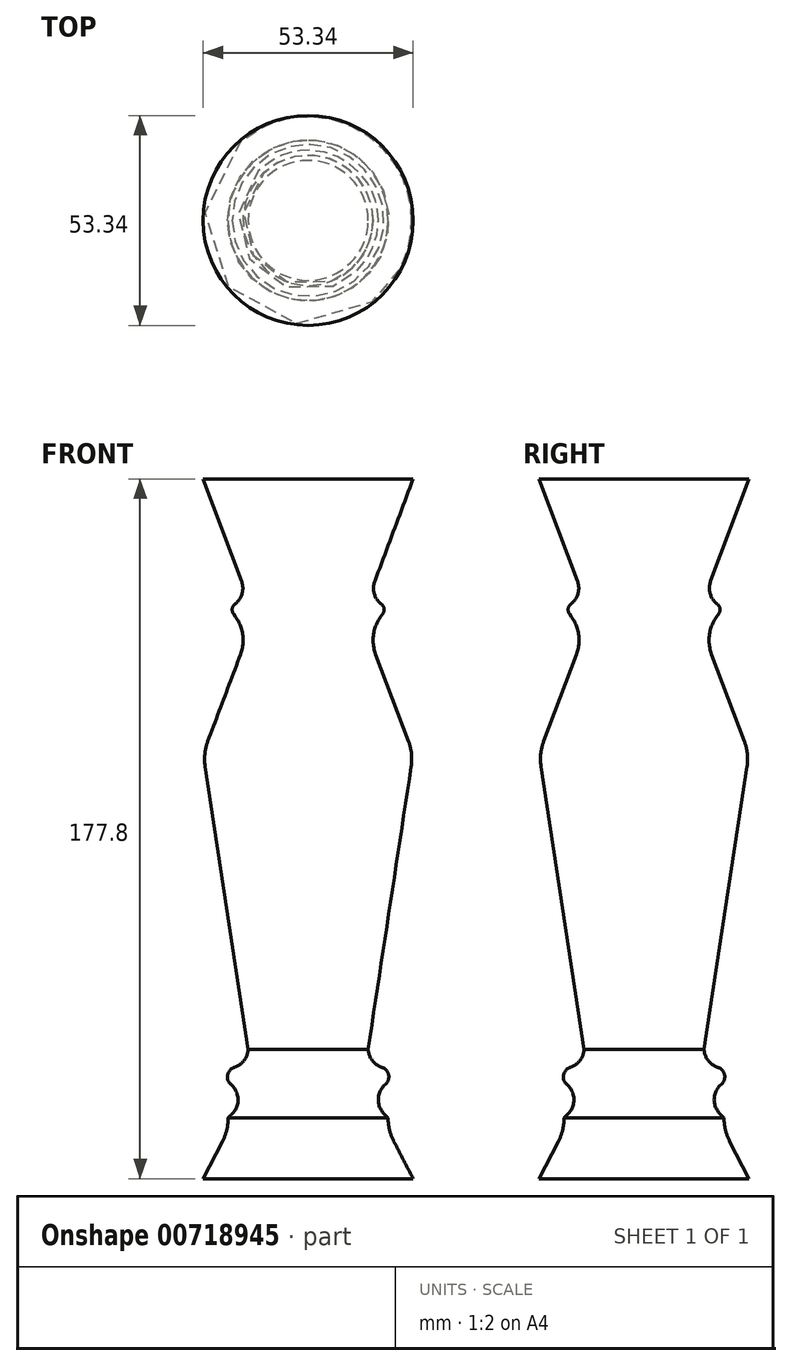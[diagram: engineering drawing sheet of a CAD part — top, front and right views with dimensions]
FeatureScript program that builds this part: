
annotation { "Feature Type Name" : "Feature", "Feature Type Description" : "" }
export const myFeature = defineFeature(function(context is Context, id is Id, definition is map)
    precondition{}
    {
        {
            var Q0;
            Q0=qCreatedBy(makeId("Front.planeOp"),FACE);
            var sketch = newSketch(context, id + "F0", { "sketchPlane" : qUnion([Q0])});
            skLineSegment(sketch, "E0", {"start": v(0, 90.6) * mm, "end": v(26.67, 90.6) * mm});
            skLineSegment(sketch, "E1", {"start": v(26.67, 90.6) * mm, "end": v(15.24, 60.11) * mm});
            skLineSegment(sketch, "E2", {"start": v(15.24, 60.11) * mm, "end": v(20.32, 58.2) * mm});
            skLineSegment(sketch, "E3", {"start": v(20.32, 58.2) * mm, "end": v(15.24, 51.1) * mm});
            skLineSegment(sketch, "E4", {"start": v(15.24, 51.1) * mm, "end": v(25.5, 23.91) * mm});
            skLineSegment(sketch, "E5", {"start": v(26.17, 17.52) * mm, "end": v(15.24, -54.38) * mm});
            skLineSegment(sketch, "E6", {"start": v(15.24, -54.38) * mm, "end": v(15.24, -54.38) * mm});
            skLineSegment(sketch, "E7", {"start": v(15.24, -54.38) * mm, "end": v(15.24, -59.17) * mm});
            skLineSegment(sketch, "E8", {"start": v(15.24, -59.17) * mm, "end": v(21.59, -59.17) * mm});
            skLineSegment(sketch, "E9", {"start": v(21.59, -59.17) * mm, "end": v(21.59, -61.6) * mm});
            skLineSegment(sketch, "E10", {"start": v(21.59, -61.6) * mm, "end": v(15.24, -67) * mm});
            skLineSegment(sketch, "E11", {"start": v(15.24, -67) * mm, "end": v(20.32, -71.7) * mm});
            skLineSegment(sketch, "E12", {"start": v(20.32, -71.7) * mm, "end": v(20.32, -71.86) * mm});
            skLineSegment(sketch, "E13", {"start": v(21.74, -77.7) * mm, "end": v(26.67, -87.2) * mm});
            skLineSegment(sketch, "E14", {"start": v(26.67, -87.2) * mm, "end": v(0, -87.2) * mm});
            skPoint(sketch, "E15.visualSharp", {"position": v(26.67, 20.8) * mm});
            skArc(sketch, "E15.filletArc", {"start": v(26.17, 17.52) * mm, "mid": v(26.25, 20.76) * mm, "end": v(25.5, 23.91) * mm});
            skPoint(sketch, "E16.visualSharp", {"position": v(20.32, -74.95) * mm});
            skArc(sketch, "E16.filletArc", {"start": v(20.32, -71.86) * mm, "mid": v(20.68, -74.86) * mm, "end": v(21.74, -77.7) * mm});
            skLineSegment(sketch, "E17", {"start": v(0, 90.6) * mm, "end": v(0, -87.2) * mm});
            skSolve(sketch);
        }
        {
            var Q0;
            Q0 = qSketchRegion(id + "F0", true);
            var Q1;
            Q1=sQuery(id+"F0.wireOp",EDGE,"E17");
            revolve(context, id + "F1", {"surfaceOperationType" : NewSurfaceOperationType.NEW, "entities" : qUnion([Q0]), "axis" : qUnion([Q1]), "revolveType" : RevolveType.FULL});
        }
        {
            var Q0;
            Q0=makeQuery(id+"F1.opRevolve","SWEPT_EDGE",EDGE,{"disambiguationData":[OSD([sQuery(id+"F0.wireOp",EDGE,"E2"),sQuery(id+"F0.wireOp",EDGE,"E3")])]});
            fillet(context, id + "F2", {"entities" : qUnion([Q0]), "radius" : 1.78 * mm, "tangentPropagation" : true, "allowEdgeOverflow" : false});
        }
        {
            var Q0;
            Q0=makeQuery(id+"F1.opRevolve","SWEPT_EDGE",EDGE,{"disambiguationData":[OSD([sQuery(id+"F0.wireOp",EDGE,"E1"),sQuery(id+"F0.wireOp",EDGE,"E2")])]});
            fillet(context, id + "F3", {"entities" : qUnion([Q0]), "radius" : 5.08 * mm, "tangentPropagation" : true, "allowEdgeOverflow" : false});
        }
        {
            var Q0;
            Q0=makeQuery(id+"F1.opRevolve","SWEPT_EDGE",EDGE,{"disambiguationData":[OSD([sQuery(id+"F0.wireOp",EDGE,"E3"),sQuery(id+"F0.wireOp",EDGE,"E4")])]});
            fillet(context, id + "F4", {"entities" : qUnion([Q0]), "radius" : 10.16 * mm, "tangentPropagation" : true, "allowEdgeOverflow" : false});
        }
        {
            var Q0;
            Q0=makeQuery(id+"F1.opRevolve","SWEPT_EDGE",EDGE,{"disambiguationData":[OSD([sQuery(id+"F0.wireOp",EDGE,"E7"),sQuery(id+"F0.wireOp",EDGE,"E8")])]});
            fillet(context, id + "F5", {"entities" : qUnion([Q0]), "radius" : 5.08 * mm, "tangentPropagation" : true, "allowEdgeOverflow" : false});
        }
        {
            var Q0;
            Q0=makeQuery(id+"F1.opRevolve","SWEPT_EDGE",EDGE,{"disambiguationData":[OSD([sQuery(id+"F0.wireOp",EDGE,"E8"),sQuery(id+"F0.wireOp",EDGE,"E9")])]});
            fillet(context, id + "F6", {"entities" : qUnion([Q0]), "radius" : 5.08 * mm, "tangentPropagation" : true, "allowEdgeOverflow" : false});
        }
        {
            var Q0;
            Q0=makeQuery(id+"F6.opFillet","BLEND_EDGE",EDGE,{"blendedFrom":[makeQuery(id+"F1.opRevolve","SWEPT_EDGE",EDGE,{"disambiguationData":[OSD([sQuery(id+"F0.wireOp",EDGE,"E8"),sQuery(id+"F0.wireOp",EDGE,"E9")])]}),makeQuery(id+"F1.opRevolve","SWEPT_FACE",FACE,{"disambiguationData":[OSD([sQuery(id+"F0.wireOp",EDGE,"E10")])]})],"blendedInto":[makeQuery(id+"F1.opRevolve","SWEPT_FACE",FACE,{"disambiguationData":[OSD([sQuery(id+"F0.wireOp",EDGE,"E10")])]})]});
            fillet(context, id + "F7", {"entities" : qUnion([Q0]), "radius" : 2.54 * mm, "tangentPropagation" : true, "allowEdgeOverflow" : false});
        }
        {
            var Q0;
            Q0=makeQuery(id+"F1.opRevolve","SWEPT_EDGE",EDGE,{"disambiguationData":[OSD([sQuery(id+"F0.wireOp",EDGE,"E10"),sQuery(id+"F0.wireOp",EDGE,"E11")])]});
            fillet(context, id + "F8", {"entities" : qUnion([Q0]), "radius" : 5.08 * mm, "tangentPropagation" : true, "allowEdgeOverflow" : false});
        }
    });
